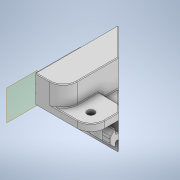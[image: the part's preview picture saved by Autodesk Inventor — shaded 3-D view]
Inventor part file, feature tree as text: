
AUTODESK INVENTOR PART (.ipt)
format: ipt  version: 2020 (Build 240168000, 168)  size: 581,120 bytes
history: native  units: in
note: dims shown in document units (in); Inventor stores cm internally (conversion verified against a paired STEP export)
features: reference x27, extrude x11, sketch x11, chamfer x3, other x3, fillet x2, plane x1
ambient origin geometry x8: Origin, YZ Plane, XZ Plane, XY Plane, X Axis, Y Axis, Z Axis, Center Point
bodies: Solid1 (feature_tree)
feature tree (58):
  extrude  "Extrusion1"  Depth=3.0in TaperAngle=0.0deg
  plane  "Work Plane1"
  extrude  "Extrusion2"  Depth=0.0098in
  extrude  "Extrusion3"  Depth=1.0in
  extrude  "Extrusion4"  Depth=1.25in
  chamfer  "Chamfer1"  Distance=1.0in
  extrude  "Extrusion5"  Depth=0.25in
  extrude  "Extrusion6"  Depth=0.25in TaperAngle=45.0deg
  extrude  "Extrusion7"  Depth=0.125in
  fillet  "Fillet1"  Radius=2.0in
  chamfer  "Chamfer2"  Distance=1.0in
  extrude  "Extrusion8"  Depth=0.2656in
  extrude  "Extrusion9"  Depth=0.5in
  extrude  "Extrusion10"  Depth=0.5in
  extrude  "Extrusion11"  TaperAngle=0.0deg  [1 undecoded]
  fillet  "Fillet2"  Radius=0.5in
  chamfer  "Chamfer3"  Distance=0.025in Angle=45.0deg
  sketch  "Sketch1"  dims[d0=1.0in d1=3.0in d2=0.0in]
  reference  "Reference1"
  reference  "Reference2"
  reference  "Reference3"
  reference  "Reference4"
  reference  "Reference5"
  reference  "Reference6"
  reference  "Reference7"
  reference  "Reference8"
  reference  "Reference9"
  reference  "Reference10"
  reference  "Reference11"
  reference  "Reference12"
  reference  "Reference13"
  reference  "Reference14"
  sketch  "Sketch2"  dims[d3=0.0098in d4=0.0098in]
  reference  "Reference15"
  reference  "Reference16"
  reference  "Reference17"
  reference  "Reference18"
  reference  "Reference19"
  reference  "Reference20"
  reference  "Reference21"
  reference  "Reference22"
  reference  "Reference23"
  reference  "Reference24"
  reference  "Reference25"
  reference  "Reference26"
  reference  "Reference27"
  sketch  "Sketch3"  dims[d5=1.0in d6=1.0in]
  sketch  "Sketch4"  dims[d7=3.0in d8=0.0in d9=1.25in]
  sketch  "Sketch5"  dims[d10=0.25in d11=1.0in d12=0.0in]
  sketch  "Sketch7"  dims[d13=1.25in d14=0.25in]
  sketch  "Sketch8"  dims[d15=1.0in d16=0.0in d17=0.25in d18=0.125in d19=45.0deg]
  sketch  "Sketch9"  dims[d20=0.0in d21=0.0in d22=0.125in d23=2.0in]
  sketch  "Sketch10"  dims[d24=0.2656in]
  sketch  "Sketch11"  dims[d25=0.5in]
  sketch  "Sketch12"  dims[d26=0.5in d27=1.0in d28=0.0in d29=0.2656in d30=0.5in d31=0.5in d32=0.0in d33=0.0in d34=0.5in d35=0.025in d36=0.125in d37=45.0deg d38=0.125in d39=0.0in d40=0.125in d41=0.0in d42=0.6in d43=0.725in d44=0.0in d45=0.6in d46=0.725in d47=0.0in d48=0.025in d49=0.02in d50=0.125in d51=45.0deg]
  other  "Assembly1"
  other  "1003-9-CL:2"
  other  "1003-9-CL:1"
note: 1 required parameter value undecoded (feature->parameter linkage not recoverable at this tier; creation-order binding heuristic only, values carry confidence <= 0.55)
